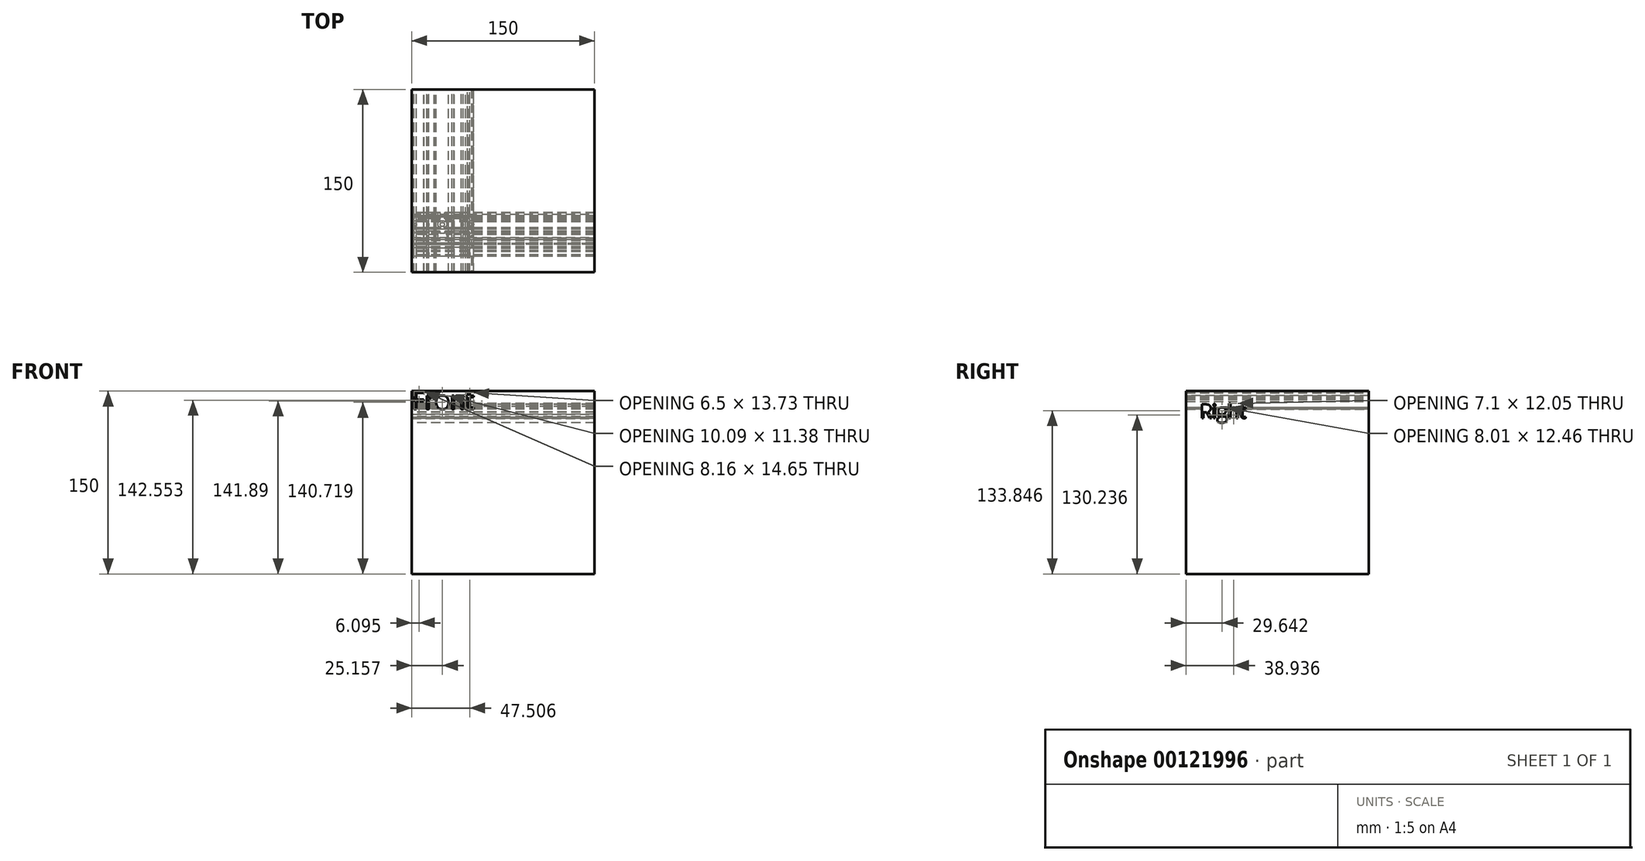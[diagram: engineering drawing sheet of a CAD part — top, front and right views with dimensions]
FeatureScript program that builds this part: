
annotation { "Feature Type Name" : "Feature", "Feature Type Description" : "" }
export const myFeature = defineFeature(function(context is Context, id is Id, definition is map)
    precondition{}
    {
        {
            var Q0;
            Q0=qCreatedBy(makeId("Front.planeOp"),FACE);
            var sketch = newSketch(context, id + "F0", { "sketchPlane" : qUnion([Q0])});
            skLineSegment(sketch, "E0.bottom", {"start": v(75, 75) * mm, "end": v(-75, 75) * mm});
            skLineSegment(sketch, "E0.top", {"start": v(75, -75) * mm, "end": v(-75, -75) * mm});
            skLineSegment(sketch, "E0.left", {"start": v(75, 75) * mm, "end": v(75, -75) * mm});
            skLineSegment(sketch, "E0.right", {"start": v(-75, 75) * mm, "end": v(-75, -75) * mm});
            skPoint(sketch, "E0.middle", {"position": v(0, 0) * mm});
            skText(sketch, "E1", { "text": "Front", "fontName": "OpenSans-Regular.ttf"});
            const initialGuessF0  = {"E1": [-0.075, 0.06023, 1, 0, 0.01477]};
            skSetInitialGuess(sketch, initialGuessF0);
            skSolve(sketch);
        }
        {
            var Q0;
            Q0=qCreatedBy(makeId("Right.planeOp"),FACE);
            var sketch = newSketch(context, id + "F1", { "sketchPlane" : qUnion([Q0])});
            skLineSegment(sketch, "E2.bottom", {"start": v(-75, 75) * mm, "end": v(75, 75) * mm});
            skLineSegment(sketch, "E2.top", {"start": v(-75, -75) * mm, "end": v(75, -75) * mm});
            skLineSegment(sketch, "E2.left", {"start": v(-75, 75) * mm, "end": v(-75, -75) * mm});
            skLineSegment(sketch, "E2.right", {"start": v(75, 75) * mm, "end": v(75, -75) * mm});
            skPoint(sketch, "E2.middle", {"position": v(0, 0) * mm});
            skText(sketch, "E3", { "text": "Right", "fontName": "OpenSans-Regular.ttf"});
            const initialGuessF1  = {"E3": [-0.06348, 0.05282, 1, 0, 0.01142]};
            skSetInitialGuess(sketch, initialGuessF1);
            skSolve(sketch);
        }
        {
            var Q0;
            Q0=makeQuery(id+"F0.imprint","IMPRINT",FACE,{"disambiguationData":[TD([[makeQuery(id+"F0.imprint","IMPRINT",EDGE,{"derivedFrom":sQuery(id+"F0.wireOp",EDGE,"E0.bottom")}),1.0]])]});
            extrude(context, id + "F2", {"entities" : qUnion([Q0]), "endBound" : BoundingType.SYMMETRIC, "depth" : 150 * mm});
        }
        {
            var Q0;
            Q0 = qSketchRegion(id + "F1", true);
            extrude(context, id + "F3", {"entities" : qUnion([Q0]), "operationType" : NewBodyOperationType.INTERSECT, "endBound" : BoundingType.SYMMETRIC, "depth" : 150 * mm});
        }
    });
